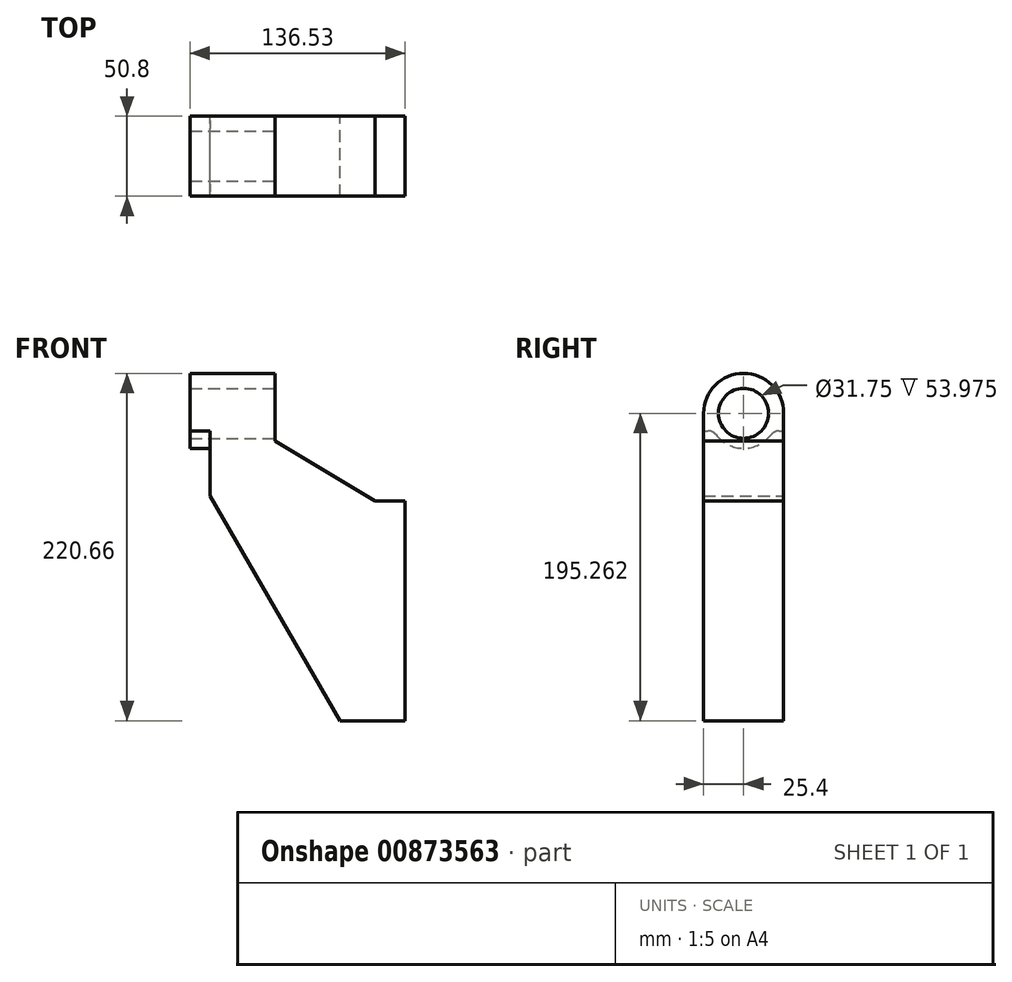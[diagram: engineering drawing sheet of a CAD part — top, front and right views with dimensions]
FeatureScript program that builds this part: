
annotation { "Feature Type Name" : "Feature", "Feature Type Description" : "" }
export const myFeature = defineFeature(function(context is Context, id is Id, definition is map)
    precondition{}
    {
        {
            var Q0;
            Q0=qCreatedBy(makeId("Front.planeOp"),FACE);
            var sketch = newSketch(context, id + "F0", { "sketchPlane" : qUnion([Q0])});
            skLineSegment(sketch, "E0", {"start": v(0, 0) * mm, "end": v(-41.28, 0) * mm});
            skLineSegment(sketch, "E1", {"start": v(0, 0) * mm, "end": v(0, 139.7) * mm});
            skLineSegment(sketch, "E2", {"start": v(0, 139.7) * mm, "end": v(-19.05, 139.7) * mm});
            skLineSegment(sketch, "E3", {"start": v(0, 139.7) * mm, "end": v(-82.55, 139.7) * mm, "construction": true});
            skLineSegment(sketch, "E4", {"start": v(-82.55, 139.7) * mm, "end": v(-82.55, 177.8) * mm, "construction": true});
            skLineSegment(sketch, "E5", {"start": v(-19.05, 139.7) * mm, "end": v(-82.55, 177.8) * mm});
            skLineSegment(sketch, "E6", {"start": v(-82.55, 177.8) * mm, "end": v(-82.55, 195.26) * mm});
            skLineSegment(sketch, "E7", {"start": v(-82.55, 195.26) * mm, "end": v(-136.53, 195.26) * mm});
            skLineSegment(sketch, "E8", {"start": v(-136.53, 195.26) * mm, "end": v(-136.53, 184.15) * mm});
            skLineSegment(sketch, "E9", {"start": v(-136.53, 184.15) * mm, "end": v(-123.83, 184.15) * mm});
            skLineSegment(sketch, "E10", {"start": v(-123.82, 184.15) * mm, "end": v(-123.82, 142.88) * mm});
            skLineSegment(sketch, "E11", {"start": v(-123.83, 142.88) * mm, "end": v(-41.27, 0) * mm});
            skSolve(sketch);
        }
        {
            var Q0;
            Q0=makeQuery(id+"F0.imprint","IMPRINT",FACE,{"disambiguationData":[TD([[makeQuery(id+"F0.imprint","IMPRINT",EDGE,{"derivedFrom":sQuery(id+"F0.wireOp",EDGE,"E0")}),-1.0]])]});
            extrude(context, id + "F1", {"entities" : qUnion([Q0]), "depth" : 50.8 * mm, "offsetDistance" : 25.4 * mm});
        }
        {
            var Q0;
            Q0=makeQuery(id+"F1.opExtrude","SWEPT_FACE",FACE,{"disambiguationData":[OSD([sQuery(id+"F0.wireOp",EDGE,"E6")])]});
            var sketch = newSketch(context, id + "F2", { "sketchPlane" : qUnion([Q0])});
            skCircle(sketch, "E12", {"center": v(-25.4, 195.26) * mm, "radius": 25.4 * mm});
            skSolve(sketch);
        }
        {
            var Q0;
            {var subQ1=sQuery(id+"F0.wireOp",EDGE,"E6");var subQ2=makeQuery(id+"F1.opExtrude","SWEPT_EDGE",EDGE,{"disambiguationData":[OSD([subQ1,sQuery(id+"F0.wireOp",EDGE,"E7")])]});Q0=makeQuery(id+"F2.imprint","IMPRINT",FACE,{"disambiguationData":[TD([[makeQuery(id+"F2.imprint","IMPRINT",EDGE,{"derivedFrom":subQ2}),1.0]])]});}
            var Q1;
            Q1=makeQuery(id+"F1.opExtrude","SWEPT_FACE",FACE,{"disambiguationData":[OSD([sQuery(id+"F0.wireOp",EDGE,"E8")])]});
            extrude(context, id + "F3", {"entities" : qUnion([Q0]), "operationType" : NewBodyOperationType.ADD, "endBound" : BoundingType.UP_TO_SURFACE, "oppositeDirection" : true, "depth" : 25.4 * mm, "endBoundEntityFace" : qUnion([Q1]), "offsetDistance" : 25.4 * mm});
        }
        {
            var Q0;
            {var subQ0=sQuery(id+"F0.wireOp",EDGE,"E8");Q0=makeQuery(id+"F3.boolean.opBoolean","MERGE",FACE,{"derivedFrom":[makeQuery(id+"F1.opExtrude","SWEPT_FACE",FACE,{"disambiguationData":[OSD([subQ0])]}),makeQuery(id+"F3.opExtrude","CAP_FACE",FACE,{"disambiguationData":[OSD([subQ0])],"isStart":false})]});}
            var sketch = newSketch(context, id + "F4", { "sketchPlane" : qUnion([Q0])});
            skCircle(sketch, "E13", {"center": v(25.4, 195.26) * mm, "radius": 22.23 * mm});
            skSolve(sketch);
        }
        {
            var Q0;
            Q0 = qSketchRegion(id + "F4", true);
            var Q1;
            Q1=makeQuery(id+"F1.opExtrude","SWEPT_FACE",FACE,{"disambiguationData":[OSD([sQuery(id+"F0.wireOp",EDGE,"E10")])]});
            extrude(context, id + "F5", {"entities" : qUnion([Q0]), "operationType" : NewBodyOperationType.ADD, "endBound" : BoundingType.UP_TO_SURFACE, "oppositeDirection" : true, "depth" : 25.4 * mm, "endBoundEntityFace" : qUnion([Q1]), "offsetDistance" : 25.4 * mm});
        }
        {
            var Q0;
            Q0=makeQuery(id+"F5.boolean.opBoolean","INTERSECT",EDGE,{"disambiguationData":[OD(0.0)],"derivedFrom":[makeQuery(id+"F1.opExtrude","SWEPT_FACE",FACE,{"disambiguationData":[OSD([sQuery(id+"F0.wireOp",EDGE,"E9")])]}),makeQuery(id+"F5.opExtrude","SWEPT_FACE",FACE,{"disambiguationData":[OSD([sQuery(id+"F4.wireOp",EDGE,"E13")])]})]});
            var Q1;
            Q1=makeQuery(id+"F5.boolean.opBoolean","INTERSECT",EDGE,{"disambiguationData":[OD(1.0)],"derivedFrom":[makeQuery(id+"F1.opExtrude","SWEPT_FACE",FACE,{"disambiguationData":[OSD([sQuery(id+"F0.wireOp",EDGE,"E9")])]}),makeQuery(id+"F5.opExtrude","SWEPT_FACE",FACE,{"disambiguationData":[OSD([sQuery(id+"F4.wireOp",EDGE,"E13")])]})]});
            fillet(context, id + "F6", {"entities" : qUnion([Q0, Q1]), "radius" : 6.35 * mm, "tangentPropagation" : true, "allowEdgeOverflow" : false});
        }
        {
            var Q0;
            {var subQ0=sQuery(id+"F0.wireOp",EDGE,"E6");Q0=makeQuery(id+"F3.boolean.opBoolean","MERGE",FACE,{"derivedFrom":[makeQuery(id+"F1.opExtrude","SWEPT_FACE",FACE,{"disambiguationData":[OSD([subQ0])]}),makeQuery(id+"F3.opExtrude","CAP_FACE",FACE,{"disambiguationData":[OSD([subQ0,sQuery(id+"F0.wireOp",EDGE,"E7"),sQuery(id+"F2.wireOp",EDGE,"E12")])],"isStart":true})]});}
            var sketch = newSketch(context, id + "F7", { "sketchPlane" : qUnion([Q0])});
            skCircle(sketch, "E14", {"center": v(-25.4, 195.26) * mm, "radius": 15.88 * mm});
            skSolve(sketch);
        }
        {
            var Q0;
            Q0=makeQuery(id+"F7.imprint","IMPRINT",FACE,{"disambiguationData":[TD([[makeQuery(id+"F7.imprint","IMPRINT",EDGE,{"derivedFrom":sQuery(id+"F7.wireOp",EDGE,"E14")}),1.0]])]});
            extrude(context, id + "F8", {"entities" : qUnion([Q0]), "operationType" : NewBodyOperationType.REMOVE, "endBound" : BoundingType.THROUGH_ALL, "oppositeDirection" : true, "depth" : 25.4 * mm, "offsetDistance" : 25.4 * mm});
        }
    });
